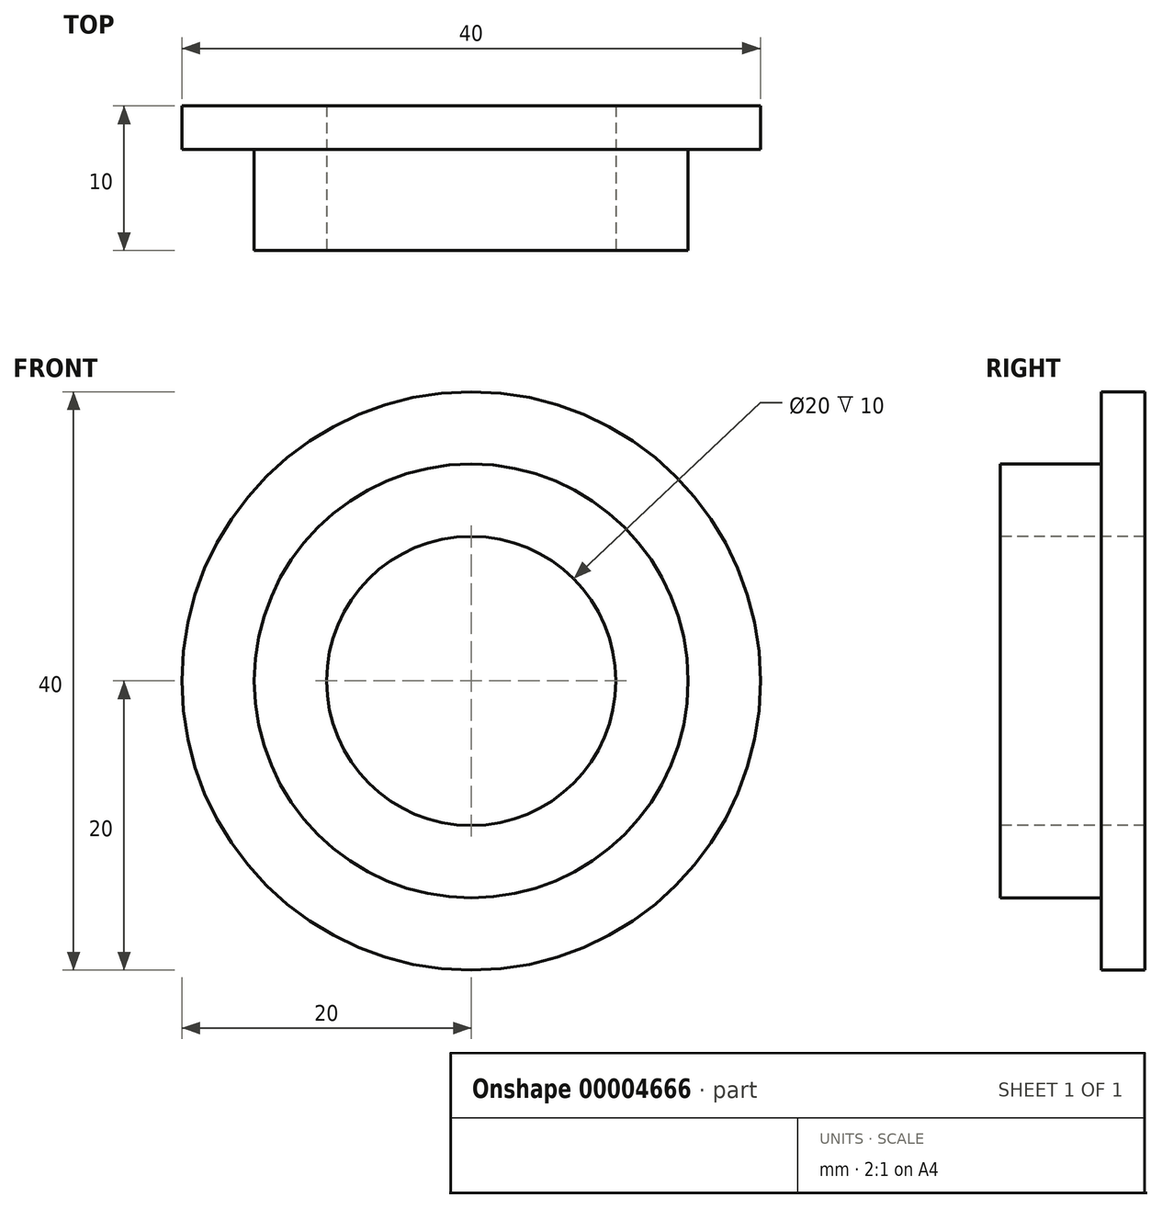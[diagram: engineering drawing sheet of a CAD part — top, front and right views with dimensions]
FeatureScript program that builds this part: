
annotation { "Feature Type Name" : "Feature", "Feature Type Description" : "" }
export const myFeature = defineFeature(function(context is Context, id is Id, definition is map)
    precondition{}
    {
        {
            var Q0;
            Q0=qCreatedBy(makeId("Top.planeOp"),FACE);
            var sketch = newSketch(context, id + "F0", { "sketchPlane" : qUnion([Q0])});
            skLineSegment(sketch, "E0", {"start": v(10, 0) * mm, "end": v(15, 0) * mm});
            skLineSegment(sketch, "E1", {"start": v(15, 0) * mm, "end": v(15, 7) * mm});
            skLineSegment(sketch, "E2", {"start": v(15, 7) * mm, "end": v(20, 7) * mm});
            skLineSegment(sketch, "E3", {"start": v(20, 7) * mm, "end": v(20, 10) * mm});
            skLineSegment(sketch, "E4", {"start": v(20, 10) * mm, "end": v(10, 10) * mm});
            skLineSegment(sketch, "E5", {"start": v(10, 10) * mm, "end": v(10, 0) * mm});
            skLineSegment(sketch, "E6", {"start": v(0, 0) * mm, "end": v(0, 10) * mm, "construction": true});
            skSolve(sketch);
        }
        {
            var Q0;
            Q0=makeQuery(id+"F0.imprint","IMPRINT",FACE,{"disambiguationData":[TD([[makeQuery(id+"F0.imprint","IMPRINT",EDGE,{"derivedFrom":sQuery(id+"F0.wireOp",EDGE,"E0")}),1.0]])]});
            var Q1;
            Q1=sQuery(id+"F0.wireOp",EDGE,"E6");
            revolve(context, id + "F1", {"entities" : qUnion([Q0]), "axis" : qUnion([Q1]), "revolveType" : RevolveType.FULL});
        }
    });
